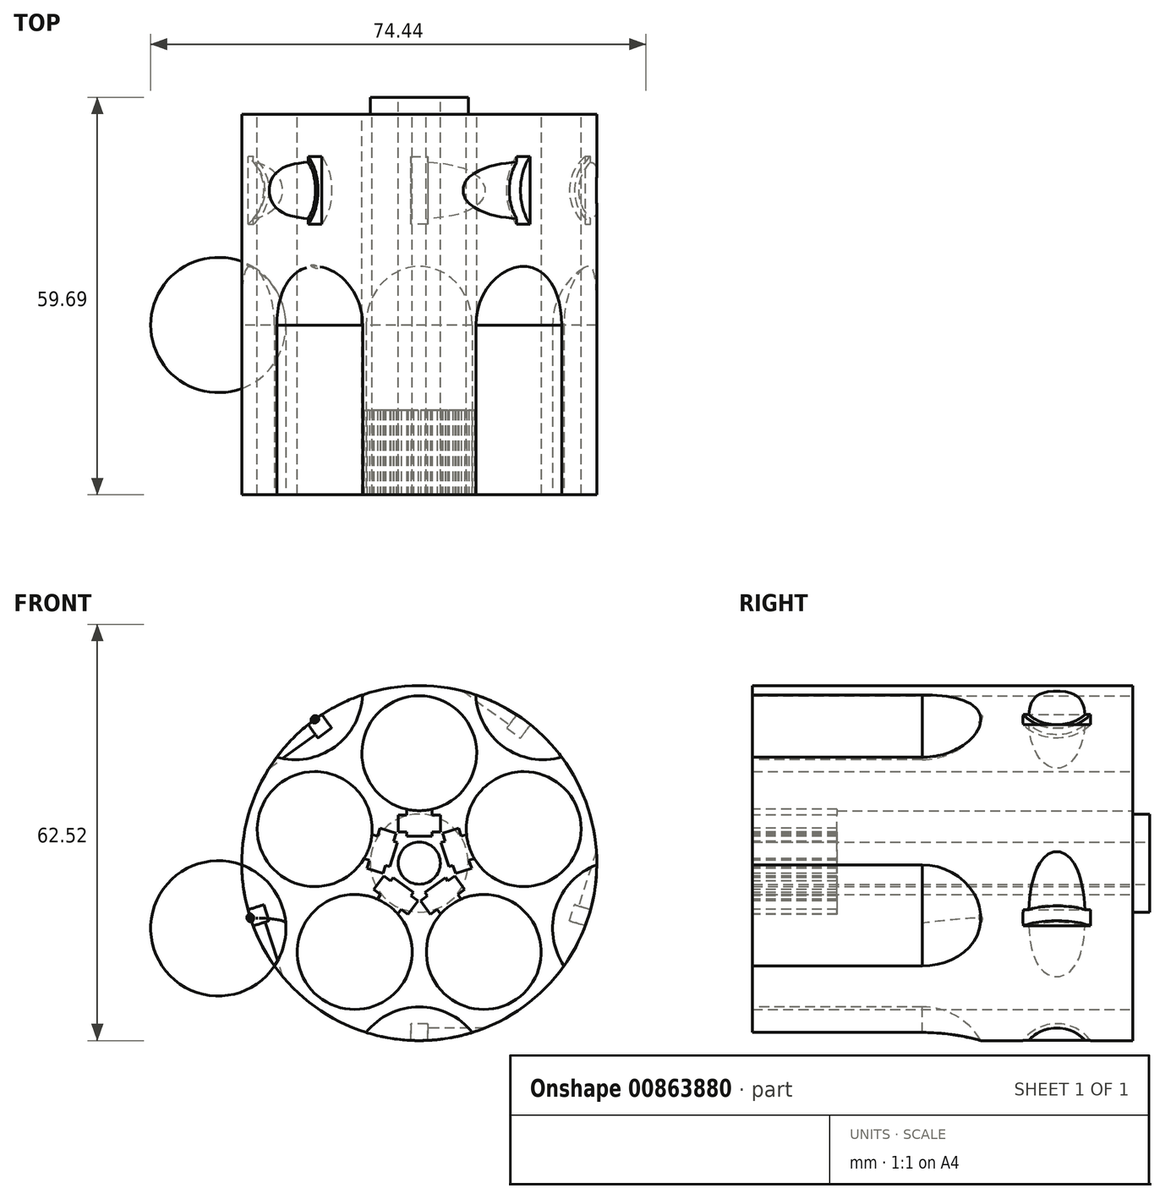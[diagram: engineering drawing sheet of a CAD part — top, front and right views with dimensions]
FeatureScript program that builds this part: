
annotation { "Feature Type Name" : "Feature", "Feature Type Description" : "" }
export const myFeature = defineFeature(function(context is Context, id is Id, definition is map)
    precondition{}
    {
        {
            var Q0;
            Q0=qCreatedBy(makeId("Front.planeOp"),FACE);
            var sketch = newSketch(context, id + "F0", { "sketchPlane" : qUnion([Q0])});
            skCircle(sketch, "E0", {"center": v(0, 0) * mm, "radius": 26.67 * mm});
            skSolve(sketch);
        }
        {
            var Q0;
            Q0=makeQuery(id+"F0.imprint","IMPRINT",FACE,{"disambiguationData":[TD([[makeQuery(id+"F0.imprint","IMPRINT",EDGE,{"derivedFrom":sQuery(id+"F0.wireOp",EDGE,"E0")}),1.0]])]});
            extrude(context, id + "F1", {"entities" : qUnion([Q0]), "depth" : 57.15 * mm, "offsetDistance" : 25.4 * mm});
        }
        {
            var Q0;
            Q0=makeQuery(id+"F1.opExtrude","CAP_FACE",FACE,{"disambiguationData":[OSD([sQuery(id+"F0.wireOp",EDGE,"E0")])],"isStart":true});
            var sketch = newSketch(context, id + "F2", { "sketchPlane" : qUnion([Q0])});
            skCircle(sketch, "E1", {"center": v(0, 16.51) * mm, "radius": 8.64 * mm});
            skCircle(sketch, "E2.1.0", {"center": v(-15.7, 5.1) * mm, "radius": 8.64 * mm});
            skCircle(sketch, "E2.2.0", {"center": v(-9.7, -13.36) * mm, "radius": 8.64 * mm});
            skCircle(sketch, "E2.3.0", {"center": v(9.7, -13.36) * mm, "radius": 8.64 * mm});
            skCircle(sketch, "E2.4.0", {"center": v(15.7, 5.1) * mm, "radius": 8.64 * mm});
            skPoint(sketch, "E2.center", {"position": v(0, 0) * mm});
            skSolve(sketch);
        }
        {
            var Q0;
            Q0 = qSketchRegion(id + "F2", true);
            extrude(context, id + "F3", {"entities" : qUnion([Q0]), "operationType" : NewBodyOperationType.REMOVE, "endBound" : BoundingType.THROUGH_ALL, "oppositeDirection" : true, "depth" : 25.4 * mm, "offsetDistance" : 25.4 * mm});
        }
        {
            var Q0;
            Q0=makeQuery(id+"F1.opExtrude","CAP_FACE",FACE,{"disambiguationData":[OSD([sQuery(id+"F0.wireOp",EDGE,"E0")])],"isStart":false});
            var sketch = newSketch(context, id + "F4", { "sketchPlane" : qUnion([Q0])});
            skCircle(sketch, "E3", {"center": v(0, -31.75) * mm, "radius": 10.16 * mm});
            skCircle(sketch, "E4.1.0", {"center": v(30.2, -9.81) * mm, "radius": 10.16 * mm});
            skCircle(sketch, "E4.2.0", {"center": v(18.66, 25.69) * mm, "radius": 10.16 * mm});
            skCircle(sketch, "E4.3.0", {"center": v(-18.66, 25.69) * mm, "radius": 10.16 * mm});
            skCircle(sketch, "E4.4.0", {"center": v(-30.2, -9.81) * mm, "radius": 10.16 * mm});
            skPoint(sketch, "E4.center", {"position": v(0, 0) * mm});
            skSolve(sketch);
        }
        {
            var Q0;
            Q0 = qSketchRegion(id + "F4", true);
            extrude(context, id + "F5", {"entities" : qUnion([Q0]), "operationType" : NewBodyOperationType.REMOVE, "oppositeDirection" : true, "depth" : 34.3 * mm, "offsetDistance" : 25.4 * mm});
        }
        {
            var Q0;
            Q0=makeQuery(id+"F5.boolean.opBoolean","COPY",EDGE,{"derivedFrom":makeQuery(id+"F5.opExtrude","CAP_EDGE",EDGE,{"disambiguationData":[OSD([sQuery(id+"F4.wireOp",EDGE,"E4.2.0")])],"isStart":false})});
            var Q1;
            Q1=makeQuery(id+"F5.boolean.opBoolean","COPY",EDGE,{"derivedFrom":makeQuery(id+"F5.opExtrude","CAP_EDGE",EDGE,{"disambiguationData":[OSD([sQuery(id+"F4.wireOp",EDGE,"E4.1.0")])],"isStart":false})});
            var Q2;
            Q2=makeQuery(id+"F5.boolean.opBoolean","COPY",EDGE,{"derivedFrom":makeQuery(id+"F5.opExtrude","CAP_EDGE",EDGE,{"disambiguationData":[OSD([sQuery(id+"F4.wireOp",EDGE,"E3")])],"isStart":false})});
            var Q3;
            Q3=makeQuery(id+"F5.boolean.opBoolean","COPY",EDGE,{"derivedFrom":makeQuery(id+"F5.opExtrude","CAP_EDGE",EDGE,{"disambiguationData":[OSD([sQuery(id+"F4.wireOp",EDGE,"E4.4.0")])],"isStart":false})});
            var Q4;
            Q4=makeQuery(id+"F5.boolean.opBoolean","COPY",EDGE,{"derivedFrom":makeQuery(id+"F5.opExtrude","CAP_EDGE",EDGE,{"disambiguationData":[OSD([sQuery(id+"F4.wireOp",EDGE,"E4.3.0")])],"isStart":false})});
            fillet(context, id + "F6", {"entities" : qUnion([Q0, Q1, Q2, Q3, Q4]), "radius" : 10.16 * mm, "tangentPropagation" : true, "allowEdgeOverflow" : false});
        }
        {
            var Q0;
            Q0=qCreatedBy(makeId("Right.planeOp"),FACE);
            var sketch = newSketch(context, id + "F7", { "sketchPlane" : qUnion([Q0])});
            skCircle(sketch, "E5", {"center": v(-11.43, -30.48) * mm, "radius": 6.35 * mm});
            skSolve(sketch);
        }
        {
            var Q0;
            Q0 = qSketchRegion(id + "F7", true);
            extrude(context, id + "F8", {"entities" : qUnion([Q0]), "operationType" : NewBodyOperationType.REMOVE, "depth" : 2.54 * mm, "offsetDistance" : 25.4 * mm, "symmetric" : true});
        }
        {
            var Q0;
            Q0=qCreatedBy(makeId("Right.planeOp"),FACE);
            var sketch = newSketch(context, id + "F9", { "sketchPlane" : qUnion([Q0])});
            skCircle(sketch, "E6", {"center": v(-11.43, -30.48) * mm, "radius": 5.72 * mm});
            skSolve(sketch);
        }
        {
            var Q0;
            Q0 = qSketchRegion(id + "F9", true);
            extrude(context, id + "F10", {"entities" : qUnion([Q0]), "operationType" : NewBodyOperationType.REMOVE, "depth" : 25.4 * mm, "offsetDistance" : 25.4 * mm});
        }
        {
            var Q0;
            Q0=qCreatedBy(makeId("Right.planeOp"),FACE);
            var sketch = newSketch(context, id + "F11", { "sketchPlane" : qUnion([Q0])});
            skLineSegment(sketch, "E7", {"start": v(-82.24, 0) * mm, "end": v(43.84, 0) * mm});
            skSolve(sketch);
        }
        {
            var Q0;
            Q0=qCreatedBy(makeId("Right.planeOp"),FACE);
            var Q1;
            Q1=sQuery(id+"F11.wireOp",EDGE,"E7");
            cPlane(context, id + "F12", {"entities" : qUnion([Q0, Q1]), "cplaneType" : CPlaneType.LINE_ANGLE, "offset" : 25.4 * mm, "angle" : 72 * degree, "width" : 152.4 * mm, "height" : 152.4 * mm});
        }
        {
            var Q0;
            Q0=qCreatedBy(id+"F12.planeOp",FACE);
            var sketch = newSketch(context, id + "F13", { "sketchPlane" : qUnion([Q0])});
            skCircle(sketch, "E8", {"center": v(-30.48, -11.43) * mm, "radius": 6.35 * mm});
            skSolve(sketch);
        }
        {
            var Q0;
            Q0 = qSketchRegion(id + "F13", true);
            extrude(context, id + "F14", {"entities" : qUnion([Q0]), "operationType" : NewBodyOperationType.REMOVE, "oppositeDirection" : true, "depth" : 2.54 * mm, "offsetDistance" : 25.4 * mm, "symmetric" : true});
        }
        {
            var Q0;
            Q0=qCreatedBy(id+"F12.planeOp",FACE);
            var sketch = newSketch(context, id + "F15", { "sketchPlane" : qUnion([Q0])});
            skCircle(sketch, "E9", {"center": v(-30.48, -11.43) * mm, "radius": 5.72 * mm});
            skSolve(sketch);
        }
        {
            var Q0;
            Q0 = qSketchRegion(id + "F15", true);
            extrude(context, id + "F16", {"entities" : qUnion([Q0]), "operationType" : NewBodyOperationType.REMOVE, "oppositeDirection" : true, "depth" : 25.4 * mm, "offsetDistance" : 25.4 * mm});
        }
        {
            var Q0;
            Q0=qCreatedBy(id+"F12.planeOp",FACE);
            var Q1;
            Q1=sQuery(id+"F11.wireOp",EDGE,"E7");
            cPlane(context, id + "F17", {"entities" : qUnion([Q0, Q1]), "cplaneType" : CPlaneType.LINE_ANGLE, "offset" : 25.4 * mm, "angle" : 72 * degree, "width" : 152.4 * mm, "height" : 152.4 * mm});
        }
        {
            var Q0;
            Q0=qCreatedBy(id+"F17.planeOp",FACE);
            var sketch = newSketch(context, id + "F18", { "sketchPlane" : qUnion([Q0])});
            skCircle(sketch, "E10", {"center": v(11.43, 30.48) * mm, "radius": 6.35 * mm});
            skSolve(sketch);
        }
        {
            var Q0;
            Q0 = qSketchRegion(id + "F18", true);
            extrude(context, id + "F19", {"entities" : qUnion([Q0]), "operationType" : NewBodyOperationType.REMOVE, "depth" : 2.54 * mm, "offsetDistance" : 25.4 * mm, "symmetric" : true});
        }
        {
            var Q0;
            Q0=qCreatedBy(id+"F17.planeOp",FACE);
            var sketch = newSketch(context, id + "F20", { "sketchPlane" : qUnion([Q0])});
            skCircle(sketch, "E11", {"center": v(11.43, 30.48) * mm, "radius": 5.72 * mm});
            skSolve(sketch);
        }
        {
            var Q0;
            Q0 = qSketchRegion(id + "F20", true);
            extrude(context, id + "F21", {"entities" : qUnion([Q0]), "operationType" : NewBodyOperationType.REMOVE, "depth" : 25.4 * mm, "offsetDistance" : 25.4 * mm});
        }
        {
            var Q0;
            Q0=qCreatedBy(id+"F17.planeOp",FACE);
            var Q1;
            Q1=sQuery(id+"F11.wireOp",EDGE,"E7");
            cPlane(context, id + "F22", {"entities" : qUnion([Q0, Q1]), "cplaneType" : CPlaneType.LINE_ANGLE, "offset" : 25.4 * mm, "angle" : 72 * degree, "width" : 152.4 * mm, "height" : 152.4 * mm});
        }
        {
            var Q0;
            Q0=qCreatedBy(id+"F22.planeOp",FACE);
            var sketch = newSketch(context, id + "F23", { "sketchPlane" : qUnion([Q0])});
            skCircle(sketch, "E12", {"center": v(-11.43, 30.48) * mm, "radius": 6.35 * mm});
            skSolve(sketch);
        }
        {
            var Q0;
            Q0 = qSketchRegion(id + "F23", true);
            extrude(context, id + "F24", {"entities" : qUnion([Q0]), "operationType" : NewBodyOperationType.REMOVE, "oppositeDirection" : true, "depth" : 2.54 * mm, "offsetDistance" : 25.4 * mm, "symmetric" : true});
        }
        {
            var Q0;
            Q0=qCreatedBy(id+"F22.planeOp",FACE);
            var sketch = newSketch(context, id + "F25", { "sketchPlane" : qUnion([Q0])});
            skCircle(sketch, "E13", {"center": v(-11.43, 30.48) * mm, "radius": 5.72 * mm});
            skSolve(sketch);
        }
        {
            var Q0;
            Q0 = qSketchRegion(id + "F25", true);
            extrude(context, id + "F26", {"entities" : qUnion([Q0]), "operationType" : NewBodyOperationType.REMOVE, "oppositeDirection" : true, "depth" : 25.4 * mm, "offsetDistance" : 25.4 * mm});
        }
        {
            var Q0;
            Q0=qCreatedBy(id+"F22.planeOp",FACE);
            var Q1;
            Q1=sQuery(id+"F11.wireOp",EDGE,"E7");
            cPlane(context, id + "F27", {"entities" : qUnion([Q0, Q1]), "cplaneType" : CPlaneType.LINE_ANGLE, "offset" : 25.4 * mm, "angle" : 72 * degree, "width" : 152.4 * mm, "height" : 152.4 * mm});
        }
        {
            var Q0;
            Q0=qCreatedBy(id+"F27.planeOp",FACE);
            var sketch = newSketch(context, id + "F28", { "sketchPlane" : qUnion([Q0])});
            skCircle(sketch, "E14", {"center": v(30.48, -11.43) * mm, "radius": 6.35 * mm});
            skSolve(sketch);
        }
        {
            var Q0;
            Q0 = qSketchRegion(id + "F28", true);
            extrude(context, id + "F29", {"entities" : qUnion([Q0]), "operationType" : NewBodyOperationType.REMOVE, "oppositeDirection" : true, "depth" : 2.54 * mm, "offsetDistance" : 25.4 * mm, "symmetric" : true});
        }
        {
            var Q0;
            Q0=qCreatedBy(id+"F27.planeOp",FACE);
            var sketch = newSketch(context, id + "F30", { "sketchPlane" : qUnion([Q0])});
            skCircle(sketch, "E15", {"center": v(30.48, -11.43) * mm, "radius": 5.72 * mm});
            skSolve(sketch);
        }
        {
            var Q0;
            Q0 = qSketchRegion(id + "F30", true);
            extrude(context, id + "F31", {"entities" : qUnion([Q0]), "operationType" : NewBodyOperationType.REMOVE, "depth" : 25.4 * mm, "offsetDistance" : 25.4 * mm});
        }
        {
            var Q0;
            Q0=makeQuery(id+"F1.opExtrude","CAP_FACE",FACE,{"disambiguationData":[OSD([sQuery(id+"F0.wireOp",EDGE,"E0")])],"isStart":true});
            var sketch = newSketch(context, id + "F32", { "sketchPlane" : qUnion([Q0])});
            skCircle(sketch, "E16", {"center": v(0, 0) * mm, "radius": 3.18 * mm});
            skSolve(sketch);
        }
        {
            var Q0;
            Q0 = qSketchRegion(id + "F32", true);
            extrude(context, id + "F33", {"entities" : qUnion([Q0]), "operationType" : NewBodyOperationType.REMOVE, "endBound" : BoundingType.THROUGH_ALL, "oppositeDirection" : true, "depth" : 25.4 * mm, "offsetDistance" : 25.4 * mm});
        }
        {
            var Q0;
            Q0=makeQuery(id+"F1.opExtrude","CAP_FACE",FACE,{"disambiguationData":[OSD([sQuery(id+"F0.wireOp",EDGE,"E0")])],"isStart":false});
            var sketch = newSketch(context, id + "F34", { "sketchPlane" : qUnion([Q0])});
            skLineSegment(sketch, "E17.bottom", {"start": v(-1.9, 8.09) * mm, "end": v(1.9, 8.09) * mm});
            skLineSegment(sketch, "E17.top", {"start": v(-1.9, 4.06) * mm, "end": v(1.9, 4.06) * mm});
            skLineSegment(sketch, "E17.left", {"start": v(-1.9, 8.09) * mm, "end": v(-1.9, 7.24) * mm});
            skLineSegment(sketch, "E17.right", {"start": v(1.9, 8.09) * mm, "end": v(1.9, 7.24) * mm});
            skLineSegment(sketch, "E18.bottom", {"start": v(-1.9, 4.7) * mm, "end": v(-3.17, 4.7) * mm});
            skLineSegment(sketch, "E18.top", {"start": v(-1.9, 7.24) * mm, "end": v(-3.18, 7.24) * mm});
            skLineSegment(sketch, "E18.right", {"start": v(-3.17, 4.7) * mm, "end": v(-3.18, 7.24) * mm});
            skPoint(sketch, "E19.firstSnap0", {"position": v(-2.54, 4.7) * mm});
            skLineSegment(sketch, "E19.bottom", {"start": v(1.9, 4.7) * mm, "end": v(3.17, 4.7) * mm});
            skLineSegment(sketch, "E19.top", {"start": v(1.9, 7.24) * mm, "end": v(3.17, 7.24) * mm});
            skLineSegment(sketch, "E19.right", {"start": v(3.17, 4.7) * mm, "end": v(3.17, 7.24) * mm});
            skLineSegment(sketch, "E20", {"start": v(0, 7.87) * mm, "end": v(0, 4.06) * mm, "construction": true});
            skLineSegment(sketch, "E21.trimOffspring", {"start": v(-1.9, 4.7) * mm, "end": v(-1.9, 4.06) * mm});
            skLineSegment(sketch, "E22.trimOffspring", {"start": v(1.9, 4.7) * mm, "end": v(1.9, 4.06) * mm});
            skLineSegment(sketch, "E23.1.0", {"start": v(-8.28, 0.69) * mm, "end": v(-7.47, 0.43) * mm});
            skLineSegment(sketch, "E23.1.1", {"start": v(-8.28, 0.69) * mm, "end": v(-7.1, 4.31) * mm});
            skLineSegment(sketch, "E23.1.2", {"start": v(-7.1, 4.31) * mm, "end": v(-6.3, 4.05) * mm});
            skLineSegment(sketch, "E23.1.3", {"start": v(-6.3, 4.05) * mm, "end": v(-5.9, 5.26) * mm});
            skLineSegment(sketch, "E23.1.4", {"start": v(-3.49, 4.47) * mm, "end": v(-5.9, 5.26) * mm});
            skLineSegment(sketch, "E23.1.5", {"start": v(-3.88, 3.26) * mm, "end": v(-3.49, 4.47) * mm});
            skLineSegment(sketch, "E23.1.6", {"start": v(-3.88, 3.26) * mm, "end": v(-3.28, 3.07) * mm});
            skLineSegment(sketch, "E23.1.7", {"start": v(-4.45, -0.56) * mm, "end": v(-3.28, 3.07) * mm});
            skLineSegment(sketch, "E23.1.8", {"start": v(-5.06, -0.36) * mm, "end": v(-4.45, -0.56) * mm});
            skLineSegment(sketch, "E23.1.9", {"start": v(-5.06, -0.36) * mm, "end": v(-5.45, -1.57) * mm});
            skLineSegment(sketch, "E23.1.10", {"start": v(-5.45, -1.57) * mm, "end": v(-7.87, -0.78) * mm});
            skLineSegment(sketch, "E23.1.11", {"start": v(-7.47, 0.43) * mm, "end": v(-7.87, -0.78) * mm});
            skLineSegment(sketch, "E23.2.0", {"start": v(-3.21, -7.66) * mm, "end": v(-2.71, -6.98) * mm});
            skLineSegment(sketch, "E23.2.1", {"start": v(-3.21, -7.66) * mm, "end": v(-6.3, -5.42) * mm});
            skLineSegment(sketch, "E23.2.2", {"start": v(-6.3, -5.42) * mm, "end": v(-5.8, -4.74) * mm});
            skLineSegment(sketch, "E23.2.3", {"start": v(-5.8, -4.74) * mm, "end": v(-6.82, -4) * mm});
            skLineSegment(sketch, "E23.2.4", {"start": v(-5.33, -1.94) * mm, "end": v(-6.82, -4) * mm});
            skLineSegment(sketch, "E23.2.5", {"start": v(-4.3, -2.68) * mm, "end": v(-5.33, -1.94) * mm});
            skLineSegment(sketch, "E23.2.6", {"start": v(-4.3, -2.68) * mm, "end": v(-3.93, -2.17) * mm});
            skLineSegment(sketch, "E23.2.7", {"start": v(-0.85, -4.4) * mm, "end": v(-3.93, -2.17) * mm});
            skLineSegment(sketch, "E23.2.8", {"start": v(-1.22, -4.92) * mm, "end": v(-0.85, -4.4) * mm});
            skLineSegment(sketch, "E23.2.9", {"start": v(-1.22, -4.92) * mm, "end": v(-0.2, -5.67) * mm});
            skLineSegment(sketch, "E23.2.10", {"start": v(-0.2, -5.67) * mm, "end": v(-1.69, -7.72) * mm});
            skLineSegment(sketch, "E23.2.11", {"start": v(-2.71, -6.98) * mm, "end": v(-1.69, -7.72) * mm});
            skLineSegment(sketch, "E23.3.0", {"start": v(6.3, -5.42) * mm, "end": v(5.8, -4.74) * mm});
            skLineSegment(sketch, "E23.3.1", {"start": v(6.3, -5.42) * mm, "end": v(3.21, -7.66) * mm});
            skLineSegment(sketch, "E23.3.2", {"start": v(3.21, -7.66) * mm, "end": v(2.71, -6.98) * mm});
            skLineSegment(sketch, "E23.3.3", {"start": v(2.71, -6.98) * mm, "end": v(1.69, -7.72) * mm});
            skLineSegment(sketch, "E23.3.4", {"start": v(0.2, -5.67) * mm, "end": v(1.69, -7.72) * mm});
            skLineSegment(sketch, "E23.3.5", {"start": v(1.22, -4.92) * mm, "end": v(0.2, -5.67) * mm});
            skLineSegment(sketch, "E23.3.6", {"start": v(1.22, -4.92) * mm, "end": v(0.85, -4.4) * mm});
            skLineSegment(sketch, "E23.3.7", {"start": v(3.93, -2.17) * mm, "end": v(0.85, -4.4) * mm});
            skLineSegment(sketch, "E23.3.8", {"start": v(4.3, -2.68) * mm, "end": v(3.93, -2.17) * mm});
            skLineSegment(sketch, "E23.3.9", {"start": v(4.3, -2.68) * mm, "end": v(5.33, -1.94) * mm});
            skLineSegment(sketch, "E23.3.10", {"start": v(5.33, -1.94) * mm, "end": v(6.82, -4) * mm});
            skLineSegment(sketch, "E23.3.11", {"start": v(5.8, -4.74) * mm, "end": v(6.82, -4) * mm});
            skLineSegment(sketch, "E23.4.0", {"start": v(7.1, 4.31) * mm, "end": v(6.3, 4.05) * mm});
            skLineSegment(sketch, "E23.4.1", {"start": v(7.1, 4.31) * mm, "end": v(8.28, 0.69) * mm});
            skLineSegment(sketch, "E23.4.2", {"start": v(8.28, 0.69) * mm, "end": v(7.47, 0.43) * mm});
            skLineSegment(sketch, "E23.4.3", {"start": v(7.47, 0.43) * mm, "end": v(7.87, -0.78) * mm});
            skLineSegment(sketch, "E23.4.4", {"start": v(5.45, -1.57) * mm, "end": v(7.87, -0.78) * mm});
            skLineSegment(sketch, "E23.4.5", {"start": v(5.06, -0.36) * mm, "end": v(5.45, -1.57) * mm});
            skLineSegment(sketch, "E23.4.6", {"start": v(5.06, -0.36) * mm, "end": v(4.45, -0.56) * mm});
            skLineSegment(sketch, "E23.4.7", {"start": v(3.28, 3.07) * mm, "end": v(4.45, -0.56) * mm});
            skLineSegment(sketch, "E23.4.8", {"start": v(3.88, 3.26) * mm, "end": v(3.28, 3.07) * mm});
            skLineSegment(sketch, "E23.4.9", {"start": v(3.88, 3.26) * mm, "end": v(3.49, 4.47) * mm});
            skLineSegment(sketch, "E23.4.10", {"start": v(3.49, 4.47) * mm, "end": v(5.9, 5.26) * mm});
            skLineSegment(sketch, "E23.4.11", {"start": v(6.3, 4.05) * mm, "end": v(5.9, 5.26) * mm});
            skPoint(sketch, "E23.center", {"position": v(0, 0) * mm});
            skSolve(sketch);
        }
        {
            var Q0;
            Q0 = qSketchRegion(id + "F34", true);
            extrude(context, id + "F35", {"entities" : qUnion([Q0]), "operationType" : NewBodyOperationType.REMOVE, "oppositeDirection" : true, "depth" : 12.7 * mm, "offsetDistance" : 25.4 * mm});
        }
        {
            var Q0;
            Q0=makeQuery(id+"F1.opExtrude","CAP_FACE",FACE,{"disambiguationData":[OSD([sQuery(id+"F0.wireOp",EDGE,"E0")])],"isStart":true});
            var sketch = newSketch(context, id + "F36", { "sketchPlane" : qUnion([Q0])});
            skCircle(sketch, "E24", {"center": v(0, 0) * mm, "radius": 7.37 * mm});
            skSolve(sketch);
        }
        {
            var Q0;
            Q0=makeQuery(id+"F36.imprint","IMPRINT",FACE,{"disambiguationData":[TD([[makeQuery(id+"F36.imprint","IMPRINT",EDGE,{"derivedFrom":sQuery(id+"F36.wireOp",EDGE,"E24")}),1.0]])]});
            extrude(context, id + "F37", {"entities" : qUnion([Q0]), "operationType" : NewBodyOperationType.ADD, "depth" : 2.54 * mm, "offsetDistance" : 25.4 * mm});
        }
    });
